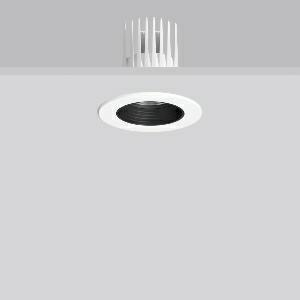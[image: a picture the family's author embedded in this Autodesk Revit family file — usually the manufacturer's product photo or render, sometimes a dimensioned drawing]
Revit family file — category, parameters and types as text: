
# Revit family: heledon_mini_e_901751_002_8527
name_source: partatom
category: Lighting Fixtures
units: mm (PartAtom-declared; Revit-internal decimal feet)

## family parameters
Cut with Voids When Loaded = No
Host = Face
Light Source = No
Part Type = Normal
Room Calculation Point = No
Round Connector Dimension = Use Diameter
Shared = No

## types (1)
- HELEDON mini E (1 x LED Modul 930, 3150 lm, 3000)
    Apparent Load = 29 VA
    Approval mark = CE
    CIE Flux Codes = 99 100 100 100 100
    Color Rendering = 90
    Color Temperature = 3000
    Default Elevation = 1800 mm
    Description = Series: HELEDON mini
Round recessed downlight. Housing: die-cast aluminium, powder-coated. Black plastic ring and recessed LED to prevent glare from the side. Optical assembly with lens made of plastic (polycarbonate) for the best homogeneous light distribution - can be changed without tools. Best colour rendering index Ra>90. Suitable for Recessed ceiling mounting. Installation without tools thanks to spring fastening system. Including separate LED converter with connecting cable 600 mm.High quality converter without flickering and stroboscopic effect. Through-wiring box (5 pole) available as accessory. The following accessories can be mounted without use of tools: interchangeable lenses, decorative glasses, honeycomb louvre, clear and frosted diffusers, white interchangeable plastic ring. 
Colour: traffic white, matt (RAL 9016)
Diameter: 124 mm
Height: 3 mm
Cut-out diameter: 114 mm
Recess height: 170 mm
Luminaire: recess height: 120 mm
Lamp: LED
Socket: without socket
Colour temperature: 3000K
Colour rendering index (CRI): 92
System power: 29 W
Rated luminous flux: 3150 lm
Luminous efficiency: 109 lm/W
Control gear: Regulated power supply
Protection class: II
Type of protection: IP 20
    Height = 0 mm  [stored 0 ft]
    Lamp = 1 x LED Modul 930
    Lamp Light Flux = 3150 lm
    Lamp count = 1
    Length = 124 mm  [stored 0.406824 ft]
    Lifetime = 50000 h
    Luminous efficacy = 109 lm/W
    Manufacturer = RZB
    ModVariant = No
    Model = 901751.002
    Mounting Place = Ceiling
    Mounting Type = Recessed
    Number of Poles = 1
    OnlyDefault = Yes
    Power Factor = 1
    Product Name = HELEDON mini E
    Product group = Recessed downlights
    ProductGroupID = 402
    Protection Class = Protection class II
    Protection Degree = IP 20
    RLX_Detail_Level = 1
    RLX_Emergency_Light_Flux = 0 lm
    RLX_Emergency_Type = 0
    RLX_Emergency_Type_DB = No
    RlxData = <blob elided: 123137 chars, md5=8f8c7d53>
    Socket = socket
    Standby Power = 0 W
    System Light Flux = 3150 lm
    System Power = 29 W
    Type Comments = Product without accessories
    Type Image = 901656.002.jpg
    URL = http://relux.com
    VarID = ---
    Voltage = 230 V
    Voltage Range = 220-240 V
    Weight = 0.00 kg
    Width = 0 mm  [stored 0 ft]

note: [stored X ft] marks values corroborated as IEEE doubles in the binary element streams (Revit-internal decimal feet)

## geometry (parser evidence)
native form markers: Blend x4, Sweep x11
no freeform markers — native parametric forms only
